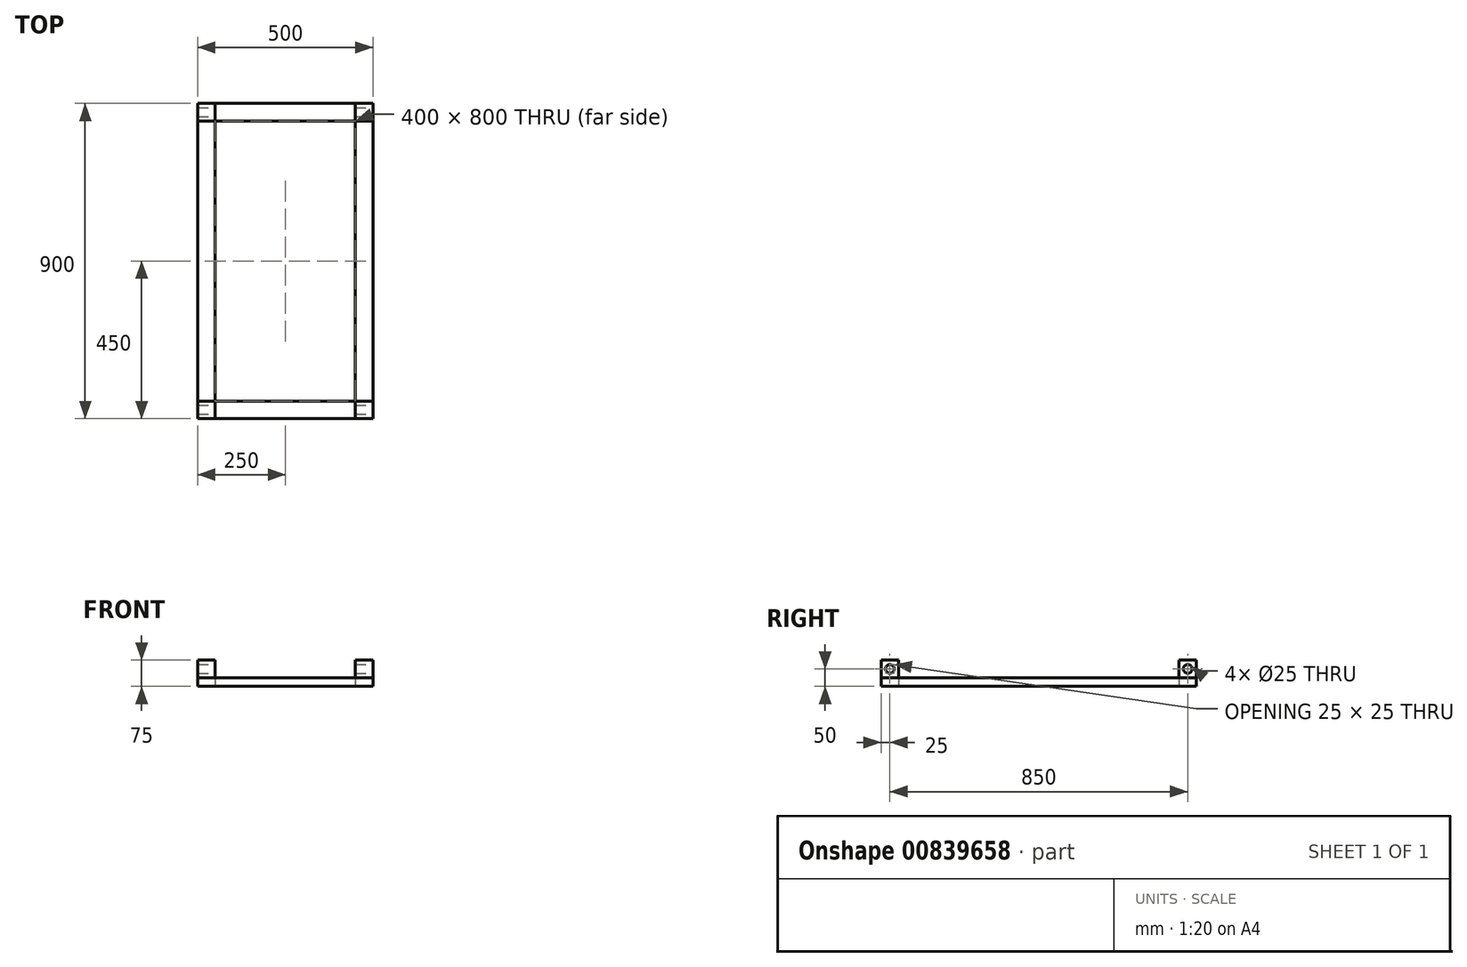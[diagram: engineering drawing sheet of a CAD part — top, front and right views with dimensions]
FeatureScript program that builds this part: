
annotation { "Feature Type Name" : "Feature", "Feature Type Description" : "" }
export const myFeature = defineFeature(function(context is Context, id is Id, definition is map)
    precondition{}
    {
        {
            var Q0;
            Q0=qCreatedBy(makeId("Top.planeOp"),FACE);
            var sketch = newSketch(context, id + "F0", { "sketchPlane" : qUnion([Q0])});
            skLineSegment(sketch, "E0.bottom", {"start": v(0, 0) * mm, "end": v(500, 0) * mm});
            skLineSegment(sketch, "E0.top", {"start": v(0, -900) * mm, "end": v(500, -900) * mm});
            skLineSegment(sketch, "E0.left", {"start": v(0, 0) * mm, "end": v(0, -900) * mm});
            skLineSegment(sketch, "E0.right", {"start": v(500, 0) * mm, "end": v(500, -900) * mm});
            skLineSegment(sketch, "E1.bottom", {"start": v(50, -50) * mm, "end": v(450, -50) * mm});
            skLineSegment(sketch, "E1.top", {"start": v(50, -850) * mm, "end": v(450, -850) * mm});
            skLineSegment(sketch, "E1.left", {"start": v(50, -50) * mm, "end": v(50, -850) * mm});
            skLineSegment(sketch, "E1.right", {"start": v(450, -50) * mm, "end": v(450, -850) * mm});
            skSolve(sketch);
        }
        {
            var Q0;
            Q0=makeQuery(id+"F0.imprint","IMPRINT",FACE,{"disambiguationData":[TD([[makeQuery(id+"F0.imprint","IMPRINT",EDGE,{"derivedFrom":sQuery(id+"F0.wireOp",EDGE,"E0.bottom")}),-1.0]])]});
            extrude(context, id + "F1", {"entities" : qUnion([Q0]), "depth" : 25 * mm, "offsetDistance" : 25 * mm});
        }
        {
            var Q0;
            Q0=makeQuery(id+"F1.opExtrude","CAP_FACE",FACE,{"disambiguationData":[OSD([sQuery(id+"F0.wireOp",EDGE,"E0.bottom"),sQuery(id+"F0.wireOp",EDGE,"E0.top"),sQuery(id+"F0.wireOp",EDGE,"E0.left"),sQuery(id+"F0.wireOp",EDGE,"E0.right"),sQuery(id+"F0.wireOp",EDGE,"E1.bottom"),sQuery(id+"F0.wireOp",EDGE,"E1.top"),sQuery(id+"F0.wireOp",EDGE,"E1.left"),sQuery(id+"F0.wireOp",EDGE,"E1.right")])],"isStart":false});
            var sketch = newSketch(context, id + "F2", { "sketchPlane" : qUnion([Q0])});
            skLineSegment(sketch, "E2.bottom", {"start": v(0, -900) * mm, "end": v(50, -900) * mm});
            skLineSegment(sketch, "E2.top", {"start": v(0, -850) * mm, "end": v(50, -850) * mm});
            skLineSegment(sketch, "E2.left", {"start": v(0, -900) * mm, "end": v(0, -850) * mm});
            skLineSegment(sketch, "E2.right", {"start": v(50, -900) * mm, "end": v(50, -850) * mm});
            skLineSegment(sketch, "E3.bottom", {"start": v(50, -50) * mm, "end": v(0, -50) * mm});
            skLineSegment(sketch, "E3.top", {"start": v(50, 0) * mm, "end": v(0, 0) * mm});
            skLineSegment(sketch, "E3.left", {"start": v(50, -50) * mm, "end": v(50, 0) * mm});
            skLineSegment(sketch, "E3.right", {"start": v(0, -50) * mm, "end": v(0, 0) * mm});
            skLineSegment(sketch, "E4.bottom", {"start": v(500, 0) * mm, "end": v(450, 0) * mm});
            skLineSegment(sketch, "E4.top", {"start": v(500, -50) * mm, "end": v(450, -50) * mm});
            skLineSegment(sketch, "E4.left", {"start": v(500, 0) * mm, "end": v(500, -50) * mm});
            skLineSegment(sketch, "E4.right", {"start": v(450, 0) * mm, "end": v(450, -50) * mm});
            skLineSegment(sketch, "E5.bottom", {"start": v(500, -900) * mm, "end": v(450, -900) * mm});
            skLineSegment(sketch, "E5.top", {"start": v(500, -850) * mm, "end": v(450, -850) * mm});
            skLineSegment(sketch, "E5.left", {"start": v(500, -900) * mm, "end": v(500, -850) * mm});
            skLineSegment(sketch, "E5.right", {"start": v(450, -900) * mm, "end": v(450, -850) * mm});
            skSolve(sketch);
        }
        {
            var Q0;
            Q0 = qSketchRegion(id + "F2", true);
            extrude(context, id + "F3", {"entities" : qUnion([Q0]), "depth" : 50 * mm, "offsetDistance" : 25 * mm});
        }
        {
            var Q0;
            Q0=makeQuery(id+"F3.opExtrude","SWEPT_FACE",FACE,{"disambiguationData":[OSD([sQuery(id+"F2.wireOp",EDGE,"E5.left")])]});
            var sketch = newSketch(context, id + "F4", { "sketchPlane" : qUnion([Q0])});
            skCircle(sketch, "E6", {"center": v(-875, 50) * mm, "radius": 12.5 * mm});
            skPoint(sketch, "E6.centerSnap0", {"position": v(-875, 75) * mm});
            skPoint(sketch, "E6.centerSnap1", {"position": v(-850, 50) * mm});
            skSolve(sketch);
        }
        {
            var Q0;
            Q0 = qSketchRegion(id + "F4", true);
            extrude(context, id + "F5", {"entities" : qUnion([Q0]), "operationType" : NewBodyOperationType.REMOVE, "endBound" : BoundingType.THROUGH_ALL, "oppositeDirection" : true, "depth" : 25 * mm, "offsetDistance" : 25 * mm});
        }
        {
            var Q0;
            Q0=makeQuery(id+"F3.opExtrude","SWEPT_FACE",FACE,{"disambiguationData":[OSD([sQuery(id+"F2.wireOp",EDGE,"E4.left")])]});
            var sketch = newSketch(context, id + "F6", { "sketchPlane" : qUnion([Q0])});
            skCircle(sketch, "E7", {"center": v(-25, 50) * mm, "radius": 12.5 * mm});
            skPoint(sketch, "E7.centerSnap0", {"position": v(0, 50) * mm});
            skPoint(sketch, "E7.centerSnap1", {"position": v(-25, 75) * mm});
            skSolve(sketch);
        }
        {
            var Q0;
            Q0 = qSketchRegion(id + "F6", true);
            extrude(context, id + "F7", {"entities" : qUnion([Q0]), "operationType" : NewBodyOperationType.REMOVE, "endBound" : BoundingType.THROUGH_ALL, "oppositeDirection" : true, "depth" : 25 * mm, "offsetDistance" : 25 * mm});
        }
    });
